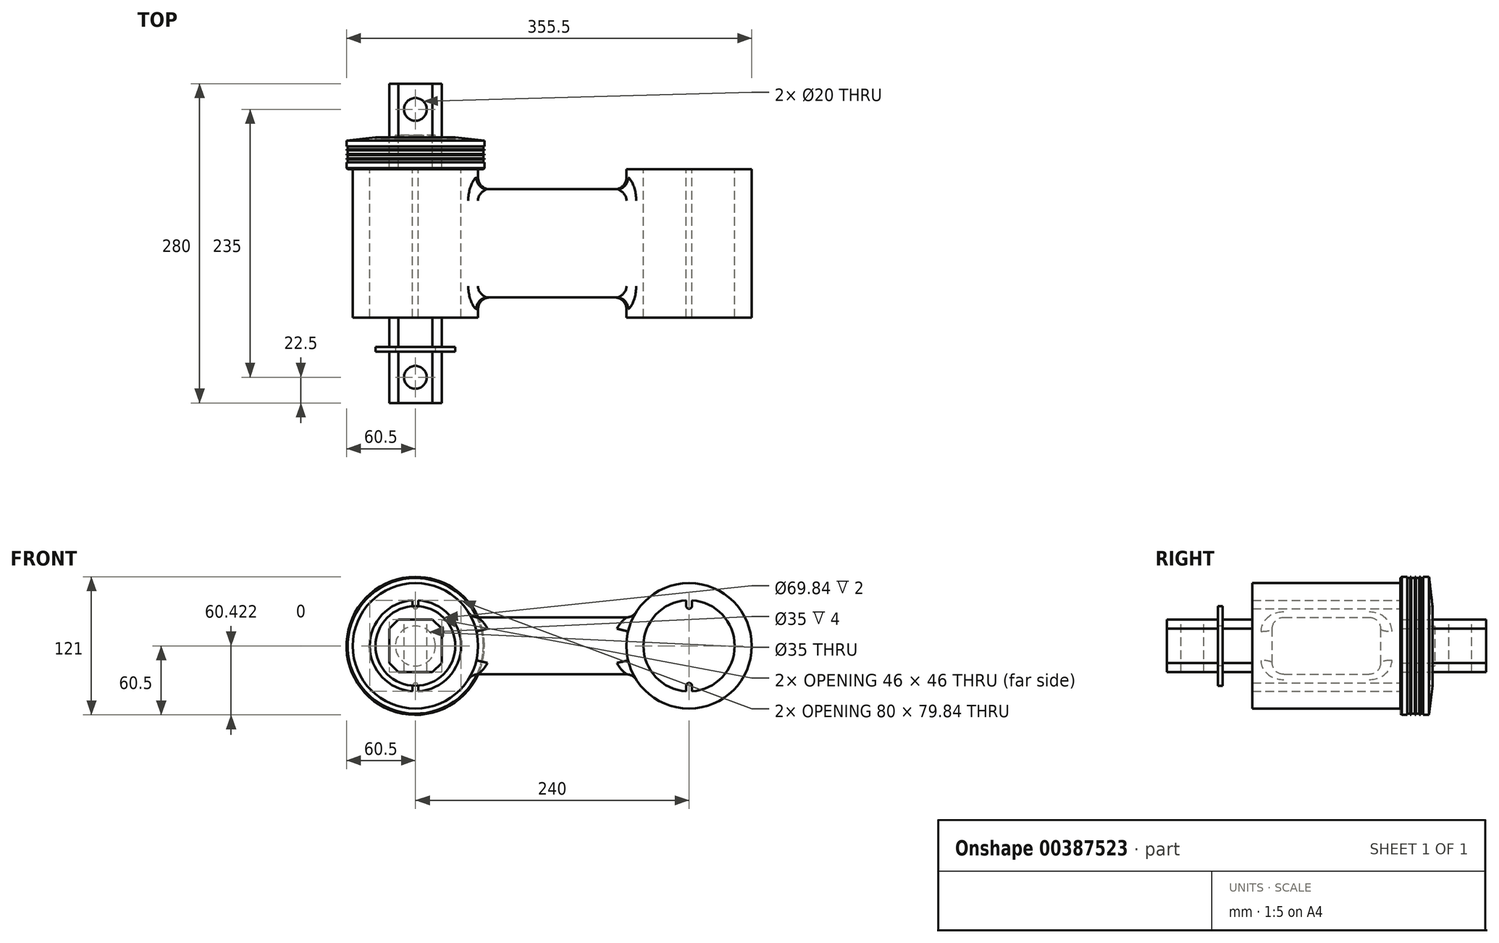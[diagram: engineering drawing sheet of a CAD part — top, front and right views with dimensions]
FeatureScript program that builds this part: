
annotation { "Feature Type Name" : "Feature", "Feature Type Description" : "" }
export const myFeature = defineFeature(function(context is Context, id is Id, definition is map)
    precondition{}
    {
        {
            var Q0;
            Q0=qCreatedBy(makeId("Front.planeOp"),FACE);
            var sketch = newSketch(context, id + "F0", { "sketchPlane" : qUnion([Q0])});
            skLineSegment(sketch, "E0", {"start": v(0, -75.22) * mm, "end": v(0, 75.8) * mm, "construction": true});
            skLineSegment(sketch, "E1.0", {"start": v(120, -75.22) * mm, "end": v(120, 75.8) * mm, "construction": true});
            skLineSegment(sketch, "E2.0", {"start": v(-120, -75.22) * mm, "end": v(-120, 75.8) * mm, "construction": true});
            skLineSegment(sketch, "E3", {"start": v(138.7, 0) * mm, "end": v(-135.83, 0) * mm, "construction": true});
            skLineSegment(sketch, "E4", {"start": v(-65.23, 25) * mm, "end": v(65.23, 25) * mm});
            skLineSegment(sketch, "E5.0", {"start": v(-65.23, -25) * mm, "end": v(65.23, -25) * mm});
            skPoint(sketch, "E6.visualSharp", {"position": v(-71.01, 25) * mm});
            skArc(sketch, "E6.filletArc", {"start": v(-73.65, 29.62) * mm, "mid": v(-70.03, 26.23) * mm, "end": v(-65.23, 25) * mm});
            skPoint(sketch, "E7.visualSharp", {"position": v(-71.01, -25) * mm});
            skArc(sketch, "E7.filletArc", {"start": v(-65.23, -25) * mm, "mid": v(-70.03, -26.23) * mm, "end": v(-73.65, -29.62) * mm});
            skPoint(sketch, "E8.visualSharp", {"position": v(71.01, 25) * mm});
            skArc(sketch, "E8.filletArc", {"start": v(65.23, 25) * mm, "mid": v(70.03, 26.23) * mm, "end": v(73.65, 29.62) * mm});
            skPoint(sketch, "E9.visualSharp", {"position": v(71.01, -25) * mm});
            skArc(sketch, "E9.filletArc", {"start": v(73.65, -29.62) * mm, "mid": v(70.03, -26.23) * mm, "end": v(65.23, -25) * mm});
            skCircle(sketch, "E10.converted", {"center": v(-120, 0) * mm, "radius": 55 * mm});
            skCircle(sketch, "E11.converted", {"center": v(120, 0) * mm, "radius": 55 * mm});
            skArc(sketch, "E12", {"start": v(-117.5, -39.92) * mm, "mid": v(-80, 0) * mm, "end": v(-117.5, 39.92) * mm});
            skArc(sketch, "E13", {"start": v(117.5, 39.92) * mm, "mid": v(80, 0) * mm, "end": v(117.5, -39.92) * mm});
            skArc(sketch, "E14", {"start": v(117.5, 35) * mm, "mid": v(120, 32.5) * mm, "end": v(122.5, 35) * mm});
            skLineSegment(sketch, "E15", {"start": v(122.5, 35) * mm, "end": v(122.5, 39.92) * mm});
            skLineSegment(sketch, "E16", {"start": v(117.5, 35) * mm, "end": v(117.5, 39.92) * mm});
            skArc(sketch, "E17.MirrorCS", {"start": v(117.5, -35) * mm, "mid": v(120, -32.5) * mm, "end": v(122.5, -35) * mm});
            skLineSegment(sketch, "E18.MirrorCS", {"start": v(122.5, -35) * mm, "end": v(122.5, -39.92) * mm});
            skLineSegment(sketch, "E19.MirrorCS", {"start": v(117.5, -35) * mm, "end": v(117.5, -39.92) * mm});
            skLineSegment(sketch, "E20.MirrorCS", {"start": v(-122.5, 35) * mm, "end": v(-122.5, 39.92) * mm});
            skLineSegment(sketch, "E21.MirrorCS", {"start": v(-117.5, 35) * mm, "end": v(-117.5, 39.92) * mm});
            skArc(sketch, "E22.MirrorCS", {"start": v(-117.5, 35) * mm, "mid": v(-120, 32.5) * mm, "end": v(-122.5, 35) * mm});
            skLineSegment(sketch, "E23.MirrorCS", {"start": v(-117.5, -35) * mm, "end": v(-117.5, -39.92) * mm});
            skArc(sketch, "E24.MirrorCS", {"start": v(-117.5, -35) * mm, "mid": v(-120, -32.5) * mm, "end": v(-122.5, -35) * mm});
            skLineSegment(sketch, "E25.MirrorCS", {"start": v(-122.5, -35) * mm, "end": v(-122.5, -39.92) * mm});
            skArc(sketch, "E26.trimOffspring", {"start": v(122.5, -39.92) * mm, "mid": v(160, 0) * mm, "end": v(122.5, 39.92) * mm});
            skArc(sketch, "E27.trimOffspring", {"start": v(-122.5, 39.92) * mm, "mid": v(-160, 0) * mm, "end": v(-122.5, -39.92) * mm});
            skSolve(sketch);
        }
        {
            var Q0;
            Q0=makeQuery(id+"F0.imprint","IMPRINT",FACE,{"disambiguationData":[TD([[makeQuery(id+"F0.imprint","IMPRINT",EDGE,{"derivedFrom":sQuery(id+"F0.wireOp",EDGE,"E12")}),-1.0]])]});
            var Q1;
            Q1=makeQuery(id+"F0.imprint","IMPRINT",FACE,{"disambiguationData":[TD([[makeQuery(id+"F0.imprint","IMPRINT",EDGE,{"derivedFrom":sQuery(id+"F0.wireOp",EDGE,"E13")}),-1.0]])]});
            extrude(context, id + "F1", {"entities" : qUnion([Q0, Q1]), "endBound" : BoundingType.SYMMETRIC, "depth" : 130 * mm});
        }
        {
            var Q0;
            Q0=makeQuery(id+"F0.imprint","IMPRINT",FACE,{"disambiguationData":[TD([[makeQuery(id+"F0.imprint","IMPRINT",EDGE,{"derivedFrom":sQuery(id+"F0.wireOp",EDGE,"E4")}),-1.0]])]});
            extrude(context, id + "F2", {"entities" : qUnion([Q0]), "operationType" : NewBodyOperationType.ADD, "endBound" : BoundingType.SYMMETRIC, "depth" : 95 * mm});
        }
        {
            var Q0;
            Q0=makeQuery(id+"F2.opExtrude","CAP_FACE",FACE,{"disambiguationData":[OSD([sQuery(id+"F0.wireOp",EDGE,"E4"),sQuery(id+"F0.wireOp",EDGE,"E5.0"),sQuery(id+"F0.wireOp",EDGE,"E6.filletArc"),sQuery(id+"F0.wireOp",EDGE,"E7.filletArc"),sQuery(id+"F0.wireOp",EDGE,"E8.filletArc"),sQuery(id+"F0.wireOp",EDGE,"E9.filletArc"),sQuery(id+"F0.wireOp",EDGE,"E10.converted"),sQuery(id+"F0.wireOp",EDGE,"E11.converted")])],"isStart":false});
            var Q1;
            Q1=makeQuery(id+"F2.opExtrude","CAP_FACE",FACE,{"disambiguationData":[OSD([sQuery(id+"F0.wireOp",EDGE,"E4"),sQuery(id+"F0.wireOp",EDGE,"E5.0"),sQuery(id+"F0.wireOp",EDGE,"E6.filletArc"),sQuery(id+"F0.wireOp",EDGE,"E7.filletArc"),sQuery(id+"F0.wireOp",EDGE,"E8.filletArc"),sQuery(id+"F0.wireOp",EDGE,"E9.filletArc"),sQuery(id+"F0.wireOp",EDGE,"E10.converted"),sQuery(id+"F0.wireOp",EDGE,"E11.converted")])],"isStart":true});
            fillet(context, id + "F3", {"entities" : qUnion([Q0, Q1]), "radius" : 10 * mm, "tangentPropagation" : true, "allowEdgeOverflow" : false});
        }
        {
            var Q0;
            Q0=qCreatedBy(makeId("Front.planeOp"),FACE);
            var sketch = newSketch(context, id + "F4", { "sketchPlane" : qUnion([Q0])});
            skArc(sketch, "E28.0", {"start": v(-117.5, -39.92) * mm, "mid": v(-80, 0) * mm, "end": v(-117.5, 39.92) * mm});
            skArc(sketch, "E28.1", {"start": v(117.5, 39.92) * mm, "mid": v(80, 0) * mm, "end": v(117.5, -39.92) * mm});
            skLineSegment(sketch, "E29.1", {"start": v(-117.5, 35) * mm, "end": v(-117.5, 39.92) * mm});
            skArc(sketch, "E29.2", {"start": v(-117.5, 35) * mm, "mid": v(-120, 32.5) * mm, "end": v(-122.5, 35) * mm});
            skLineSegment(sketch, "E29.3", {"start": v(-122.5, 35) * mm, "end": v(-122.5, 39.92) * mm});
            skArc(sketch, "E29.4", {"start": v(-122.5, 39.92) * mm, "mid": v(-160, 0) * mm, "end": v(-122.5, -39.92) * mm});
            skLineSegment(sketch, "E29.5", {"start": v(-122.5, -35) * mm, "end": v(-122.5, -39.92) * mm});
            skArc(sketch, "E29.6", {"start": v(-117.5, -35) * mm, "mid": v(-120, -32.5) * mm, "end": v(-122.5, -35) * mm});
            skLineSegment(sketch, "E29.7", {"start": v(-117.5, -35) * mm, "end": v(-117.5, -39.92) * mm});
            skLineSegment(sketch, "E30.1", {"start": v(117.5, 35) * mm, "end": v(117.5, 39.92) * mm});
            skLineSegment(sketch, "E30.2", {"start": v(122.5, 35) * mm, "end": v(122.5, 39.92) * mm});
            skArc(sketch, "E30.3", {"start": v(117.5, 35) * mm, "mid": v(120, 32.5) * mm, "end": v(122.5, 35) * mm});
            skArc(sketch, "E30.4", {"start": v(122.5, -39.92) * mm, "mid": v(160, 0) * mm, "end": v(122.5, 39.92) * mm});
            skLineSegment(sketch, "E30.5", {"start": v(122.5, -35) * mm, "end": v(122.5, -39.92) * mm});
            skArc(sketch, "E30.6", {"start": v(117.5, -35) * mm, "mid": v(120, -32.5) * mm, "end": v(122.5, -35) * mm});
            skLineSegment(sketch, "E30.7", {"start": v(117.5, -35) * mm, "end": v(117.5, -39.92) * mm});
            skSolve(sketch);
        }
        {
            var Q0;
            Q0=makeQuery(id+"F4.imprint","IMPRINT",FACE,{"disambiguationData":[TD([[makeQuery(id+"F4.imprint","IMPRINT",EDGE,{"derivedFrom":sQuery(id+"F4.wireOp",EDGE,"E28.1")}),1.0]])]});
            var Q1;
            Q1=makeQuery(id+"F4.imprint","IMPRINT",FACE,{"disambiguationData":[TD([[makeQuery(id+"F4.imprint","IMPRINT",EDGE,{"derivedFrom":sQuery(id+"F4.wireOp",EDGE,"E28.0")}),1.0]])]});
            extrude(context, id + "F5", {"entities" : qUnion([Q0, Q1]), "endBound" : BoundingType.SYMMETRIC, "depth" : 130 * mm});
        }
        {
            var Q0;
            Q0=qCreatedBy(makeId("Front.planeOp"),FACE);
            var sketch = newSketch(context, id + "F6", { "sketchPlane" : qUnion([Q0])});
            skCircle(sketch, "E31.0", {"center": v(-120, 0) * mm, "radius": 55 * mm, "construction": true});
            skCircle(sketch, "E32.0", {"center": v(120, 0) * mm, "radius": 55 * mm, "construction": true});
            skLineSegment(sketch, "E33.bottom", {"start": v(-105, -23) * mm, "end": v(-135, -23) * mm});
            skLineSegment(sketch, "E33.top", {"start": v(-105, 23) * mm, "end": v(-135, 23) * mm});
            skLineSegment(sketch, "E33.left", {"start": v(-97, -15) * mm, "end": v(-97, 15) * mm});
            skLineSegment(sketch, "E33.right", {"start": v(-143, -15) * mm, "end": v(-143, 15) * mm});
            skLineSegment(sketch, "E34", {"start": v(-120, 29.37) * mm, "end": v(-120, -29.52) * mm, "construction": true});
            skPoint(sketch, "E34.endSnap0", {"position": v(-120, 23) * mm});
            skLineSegment(sketch, "E35.0", {"start": v(-135, 29.37) * mm, "end": v(-135, -29.52) * mm, "construction": true});
            skLineSegment(sketch, "E36.0", {"start": v(-105, 29.37) * mm, "end": v(-105, -29.52) * mm, "construction": true});
            skLineSegment(sketch, "E37", {"start": v(0, 0) * mm, "end": v(0, -57.4) * mm, "construction": true});
            skLineSegment(sketch, "E38", {"start": v(-146.66, 0) * mm, "end": v(-89.7, 0) * mm, "construction": true});
            skLineSegment(sketch, "E39.0", {"start": v(-146.66, 15) * mm, "end": v(-89.7, 15) * mm, "construction": true});
            skLineSegment(sketch, "E40.0", {"start": v(-146.66, -15) * mm, "end": v(-89.7, -15) * mm, "construction": true});
            skArc(sketch, "E41.0", {"start": v(-127.46, -34.2) * mm, "mid": v(-120, -27.5) * mm, "end": v(-112.54, -34.2) * mm});
            skArc(sketch, "E41.1", {"start": v(-127.46, 34.2) * mm, "mid": v(-155, 0) * mm, "end": v(-127.46, -34.2) * mm});
            skArc(sketch, "E41.2", {"start": v(-112.54, 34.2) * mm, "mid": v(-120, 27.5) * mm, "end": v(-127.46, 34.2) * mm});
            skArc(sketch, "E41.3", {"start": v(-112.54, -34.2) * mm, "mid": v(-85, 0) * mm, "end": v(-112.54, 34.2) * mm});
            skLineSegment(sketch, "E42", {"start": v(-143, 15) * mm, "end": v(-135, 23) * mm});
            skLineSegment(sketch, "E43", {"start": v(-105, 23) * mm, "end": v(-97, 15) * mm});
            skLineSegment(sketch, "E44", {"start": v(-143, -15) * mm, "end": v(-135, -23) * mm});
            skLineSegment(sketch, "E45", {"start": v(-105, -23) * mm, "end": v(-97, -15) * mm});
            skPoint(sketch, "E46.orphan", {"position": v(-97, -23) * mm});
            skPoint(sketch, "E47.orphan", {"position": v(-97, 23) * mm});
            skPoint(sketch, "E48.orphan", {"position": v(-143, 23) * mm});
            skPoint(sketch, "E49.orphan", {"position": v(-143, -23) * mm});
            skLineSegment(sketch, "E50.MirrorCS", {"start": v(105, 23) * mm, "end": v(97, 15) * mm});
            skLineSegment(sketch, "E51.MirrorCS", {"start": v(105, -23) * mm, "end": v(97, -15) * mm});
            skLineSegment(sketch, "E52.MirrorCS", {"start": v(143, -15) * mm, "end": v(143, 15) * mm});
            skLineSegment(sketch, "E53.MirrorCS", {"start": v(105, 23) * mm, "end": v(135, 23) * mm});
            skLineSegment(sketch, "E54.MirrorCS", {"start": v(105, -23) * mm, "end": v(135, -23) * mm});
            skPoint(sketch, "E55.MirrorP", {"position": v(97, 23) * mm});
            skPoint(sketch, "E56.MirrorP", {"position": v(120, 23) * mm});
            skPoint(sketch, "E57.MirrorP", {"position": v(97, -23) * mm});
            skLineSegment(sketch, "E58.MirrorCS", {"start": v(97, -15) * mm, "end": v(97, 15) * mm});
            skLineSegment(sketch, "E59.MirrorCS", {"start": v(143, -15) * mm, "end": v(135, -23) * mm});
            skLineSegment(sketch, "E60.MirrorCS", {"start": v(143, 15) * mm, "end": v(135, 23) * mm});
            skSolve(sketch);
        }
        {
            var Q0;
            Q0=makeQuery(id+"F6.imprint","IMPRINT",FACE,{"disambiguationData":[TD([[makeQuery(id+"F6.imprint","IMPRINT",EDGE,{"derivedFrom":sQuery(id+"F6.wireOp",EDGE,"E33.bottom")}),-1.0]])]});
            extrude(context, id + "F7", {"entities" : qUnion([Q0]), "operationType" : NewBodyOperationType.ADD, "endBound" : BoundingType.SYMMETRIC, "depth" : 280 * mm});
        }
        {
            var Q0;
            Q0=makeQuery(id+"F6.imprint","IMPRINT",FACE,{"disambiguationData":[TD([[makeQuery(id+"F6.imprint","IMPRINT",EDGE,{"derivedFrom":sQuery(id+"F6.wireOp",EDGE,"E50.MirrorCS")}),1.0]])]});
            extrude(context, id + "F8", {"entities" : qUnion([Q0]), "operationType" : NewBodyOperationType.ADD, "endBound" : BoundingType.SYMMETRIC, "depth" : 280 * mm});
        }
        {
            var Q0;
            Q0=makeQuery(id+"F7.opExtrude","CAP_FACE",FACE,{"disambiguationData":[OSD([sQuery(id+"F6.wireOp",EDGE,"E33.bottom"),sQuery(id+"F6.wireOp",EDGE,"E33.top"),sQuery(id+"F6.wireOp",EDGE,"E33.left"),sQuery(id+"F6.wireOp",EDGE,"E33.right"),sQuery(id+"F6.wireOp",EDGE,"E42"),sQuery(id+"F6.wireOp",EDGE,"E43"),sQuery(id+"F6.wireOp",EDGE,"E44"),sQuery(id+"F6.wireOp",EDGE,"E45")])],"isStart":false});
            cPlane(context, id + "F9", {"entities" : qUnion([Q0]), "cplaneType" : CPlaneType.OFFSET, "offset" : 45 * mm, "oppositeDirection" : true, "width" : 150 * mm, "height" : 150 * mm});
        }
        {
            var Q0;
            Q0=qCreatedBy(id+"F9.planeOp",FACE);
            var sketch = newSketch(context, id + "F10", { "sketchPlane" : qUnion([Q0])});
            skPoint(sketch, "E61.0", {"position": v(-120, -0.08) * mm});
            skCircle(sketch, "E62", {"center": v(-120, -0.08) * mm, "radius": 35 * mm});
            skCircle(sketch, "E63", {"center": v(-120, -0.08) * mm, "radius": 17.5 * mm});
            skCircle(sketch, "E64.MirrorC", {"center": v(120, -0.08) * mm, "radius": 17.5 * mm});
            skCircle(sketch, "E65.MirrorC", {"center": v(120, -0.08) * mm, "radius": 35 * mm});
            skSolve(sketch);
        }
        {
            var Q0;
            Q0=makeQuery(id+"F10.imprint","IMPRINT",FACE,{"disambiguationData":[TD([[makeQuery(id+"F10.imprint","IMPRINT",EDGE,{"derivedFrom":sQuery(id+"F10.wireOp",EDGE,"E62")}),1.0]])]});
            extrude(context, id + "F11", {"entities" : qUnion([Q0]), "oppositeDirection" : true, "depth" : 4 * mm});
        }
        {
            var Q0;
            Q0=makeQuery(id+"F10.imprint","IMPRINT",FACE,{"disambiguationData":[TD([[makeQuery(id+"F10.imprint","IMPRINT",EDGE,{"derivedFrom":sQuery(id+"F10.wireOp",EDGE,"E64.MirrorC")}),1.0]])]});
            extrude(context, id + "F12", {"entities" : qUnion([Q0]), "oppositeDirection" : true, "depth" : 4 * mm});
        }
        {
            var Q0;
            Q0=makeQuery(id+"F8.opExtrude","CAP_FACE",FACE,{"disambiguationData":[OSD([sQuery(id+"F6.wireOp",EDGE,"E50.MirrorCS"),sQuery(id+"F6.wireOp",EDGE,"E51.MirrorCS"),sQuery(id+"F6.wireOp",EDGE,"E52.MirrorCS"),sQuery(id+"F6.wireOp",EDGE,"E53.MirrorCS"),sQuery(id+"F6.wireOp",EDGE,"E54.MirrorCS"),sQuery(id+"F6.wireOp",EDGE,"E58.MirrorCS"),sQuery(id+"F6.wireOp",EDGE,"E59.MirrorCS"),sQuery(id+"F6.wireOp",EDGE,"E60.MirrorCS")])],"isStart":true});
            cPlane(context, id + "F13", {"entities" : qUnion([Q0]), "cplaneType" : CPlaneType.OFFSET, "offset" : 45 * mm, "oppositeDirection" : true, "width" : 150 * mm, "height" : 150 * mm});
        }
        {
            var Q0;
            Q0=qCreatedBy(id+"F13.planeOp",FACE);
            var sketch = newSketch(context, id + "F14", { "sketchPlane" : qUnion([Q0])});
            skCircle(sketch, "E66.0", {"center": v(-120, -0.08) * mm, "radius": 17.5 * mm});
            skCircle(sketch, "E67.0", {"center": v(-120, -0.08) * mm, "radius": 35 * mm});
            skCircle(sketch, "E68.0", {"center": v(120, -0.08) * mm, "radius": 17.5 * mm});
            skCircle(sketch, "E69.0", {"center": v(120, -0.08) * mm, "radius": 35 * mm});
            skSolve(sketch);
        }
        {
            var Q0;
            Q0=makeQuery(id+"F14.imprint","IMPRINT",FACE,{"disambiguationData":[TD([[makeQuery(id+"F14.imprint","IMPRINT",EDGE,{"derivedFrom":sQuery(id+"F14.wireOp",EDGE,"E66.0")}),-1.0]])]});
            var Q1;
            Q1=makeQuery(id+"F14.imprint","IMPRINT",FACE,{"disambiguationData":[TD([[makeQuery(id+"F14.imprint","IMPRINT",EDGE,{"derivedFrom":sQuery(id+"F14.wireOp",EDGE,"E68.0")}),1.0]])]});
            extrude(context, id + "F15", {"entities" : qUnion([Q0, Q1]), "oppositeDirection" : true, "depth" : 4 * mm});
        }
        {
            var Q0;
            Q0=makeQuery(id+"F12.opExtrude","SWEPT_BODY",BODY,{"disambiguationData":[OSD([sQuery(id+"F10.wireOp",EDGE,"E64.MirrorC"),sQuery(id+"F10.wireOp",EDGE,"E65.MirrorC")])]});
            var Q1;
            Q1=makeQuery(id+"F15.opExtrude","SWEPT_BODY",BODY,{"disambiguationData":[OSD([sQuery(id+"F14.wireOp",EDGE,"E66.0"),sQuery(id+"F14.wireOp",EDGE,"E67.0")])]});
            var Q2;
            Q2=makeQuery(id+"F5.opExtrude","SWEPT_BODY",BODY,{"disambiguationData":[OSD([sQuery(id+"F4.wireOp",EDGE,"E28.1"),sQuery(id+"F4.wireOp",EDGE,"E30.1"),sQuery(id+"F4.wireOp",EDGE,"E30.2"),sQuery(id+"F4.wireOp",EDGE,"E30.3"),sQuery(id+"F4.wireOp",EDGE,"E30.4"),sQuery(id+"F4.wireOp",EDGE,"E30.5"),sQuery(id+"F4.wireOp",EDGE,"E30.6"),sQuery(id+"F4.wireOp",EDGE,"E30.7")])]});
            booleanBodies(context, id + "F16", {"operationType" : BooleanOperationType.SUBTRACTION, "tools" : qUnion([Q0, Q1]), "targets" : qUnion([Q2]), "keepTools" : true});
        }
        {
            var Q0;
            Q0=makeQuery(id+"F15.opExtrude","SWEPT_BODY",BODY,{"disambiguationData":[OSD([sQuery(id+"F14.wireOp",EDGE,"E68.0"),sQuery(id+"F14.wireOp",EDGE,"E69.0")])]});
            var Q1;
            Q1=makeQuery(id+"F11.opExtrude","SWEPT_BODY",BODY,{"disambiguationData":[OSD([sQuery(id+"F10.wireOp",EDGE,"E62"),sQuery(id+"F10.wireOp",EDGE,"E63")])]});
            var Q2;
            Q2=makeQuery(id+"F5.opExtrude","SWEPT_BODY",BODY,{"disambiguationData":[OSD([sQuery(id+"F4.wireOp",EDGE,"E28.0"),sQuery(id+"F4.wireOp",EDGE,"E29.1"),sQuery(id+"F4.wireOp",EDGE,"E29.2"),sQuery(id+"F4.wireOp",EDGE,"E29.3"),sQuery(id+"F4.wireOp",EDGE,"E29.4"),sQuery(id+"F4.wireOp",EDGE,"E29.5"),sQuery(id+"F4.wireOp",EDGE,"E29.6"),sQuery(id+"F4.wireOp",EDGE,"E29.7")])]});
            booleanBodies(context, id + "F17", {"operationType" : BooleanOperationType.SUBTRACTION, "tools" : qUnion([Q0, Q1]), "targets" : qUnion([Q2]), "keepTools" : true});
        }
        {
            var Q0;
            Q0=qCreatedBy(makeId("Top.planeOp"),FACE);
            var sketch = newSketch(context, id + "F18", { "sketchPlane" : qUnion([Q0])});
            skPoint(sketch, "E70.0", {"position": v(-120, -140) * mm});
            skPoint(sketch, "E71.0", {"position": v(-120, 140) * mm});
            skPoint(sketch, "E72.0", {"position": v(120, 140) * mm});
            skPoint(sketch, "E73.0", {"position": v(120, -140) * mm});
            skCircle(sketch, "E74", {"center": v(-120, 117.5) * mm, "radius": 10 * mm});
            skCircle(sketch, "E75.MirrorC", {"center": v(-120, -117.5) * mm, "radius": 10 * mm});
            skCircle(sketch, "E76.MirrorC", {"center": v(120, 117.5) * mm, "radius": 10 * mm});
            skCircle(sketch, "E77.MirrorC", {"center": v(120, -117.5) * mm, "radius": 10 * mm});
            skSolve(sketch);
        }
        {
            var Q0;
            Q0=qSketchRegion(id+"F18",true);
            var Q1;
            Q1=sQuery(id+"F18.wireOp",EDGE,"E74");
            var Q2;
            Q2=sQuery(id+"F18.wireOp",EDGE,"E76.MirrorC");
            var Q3;
            Q3=sQuery(id+"F18.wireOp",EDGE,"E77.MirrorC");
            var Q4;
            Q4=sQuery(id+"F18.wireOp",EDGE,"E75.MirrorC");
            extrude(context, id + "F19", {"entities" : qUnion([Q0]), "operationType" : NewBodyOperationType.REMOVE, "surfaceEntities" : qUnion([Q1, Q2, Q3, Q4]), "endBound" : BoundingType.SYMMETRIC, "oppositeDirection" : true, "depth" : 100 * mm});
        }
        {
            var Q0;
            {var subQ2=sQuery(id+"F6.wireOp",EDGE,"E33.right");Q0=makeQuery(id+"F17.opBoolean","SPLIT",FACE,{"disambiguationData":[TD([makeQuery(id+"F15.opExtrude","CAP_FACE",FACE,{"disambiguationData":[OSD([sQuery(id+"F14.wireOp",EDGE,"E68.0"),sQuery(id+"F14.wireOp",EDGE,"E69.0")])],"isStart":true})])],"derivedFrom":makeQuery(id+"F7.boolean.opBoolean","SPLIT",FACE,{"disambiguationData":[TD([makeQuery(id+"F5.opExtrude","CAP_FACE",FACE,{"disambiguationData":[OSD([sQuery(id+"F4.wireOp",EDGE,"E28.0"),sQuery(id+"F4.wireOp",EDGE,"E29.1"),sQuery(id+"F4.wireOp",EDGE,"E29.2"),sQuery(id+"F4.wireOp",EDGE,"E29.3"),sQuery(id+"F4.wireOp",EDGE,"E29.4"),sQuery(id+"F4.wireOp",EDGE,"E29.5"),sQuery(id+"F4.wireOp",EDGE,"E29.6"),sQuery(id+"F4.wireOp",EDGE,"E29.7")])],"isStart":true})])],"derivedFrom":makeQuery(id+"F7.opExtrude","SWEPT_FACE",FACE,{"disambiguationData":[OSD([subQ2])]})})});}
            var Q1;
            {var subQ2=sQuery(id+"F6.wireOp",EDGE,"E33.left");Q1=makeQuery(id+"F17.opBoolean","SPLIT",FACE,{"disambiguationData":[TD([makeQuery(id+"F11.opExtrude","CAP_FACE",FACE,{"disambiguationData":[OSD([sQuery(id+"F10.wireOp",EDGE,"E62"),sQuery(id+"F10.wireOp",EDGE,"E63")])],"isStart":true})])],"derivedFrom":makeQuery(id+"F7.boolean.opBoolean","SPLIT",FACE,{"disambiguationData":[TD([makeQuery(id+"F5.opExtrude","CAP_FACE",FACE,{"disambiguationData":[OSD([sQuery(id+"F4.wireOp",EDGE,"E28.0"),sQuery(id+"F4.wireOp",EDGE,"E29.1"),sQuery(id+"F4.wireOp",EDGE,"E29.2"),sQuery(id+"F4.wireOp",EDGE,"E29.3"),sQuery(id+"F4.wireOp",EDGE,"E29.4"),sQuery(id+"F4.wireOp",EDGE,"E29.5"),sQuery(id+"F4.wireOp",EDGE,"E29.6"),sQuery(id+"F4.wireOp",EDGE,"E29.7")])],"isStart":false})])],"derivedFrom":makeQuery(id+"F7.opExtrude","SWEPT_FACE",FACE,{"disambiguationData":[OSD([subQ2])]})})});}
            cPlane(context, id + "F20", {"entities" : qUnion([Q0, Q1]), "cplaneType" : CPlaneType.MID_PLANE, "offset" : 25 * mm, "width" : 150 * mm, "height" : 150 * mm});
        }
        {
            var Q0;
            Q0=qCreatedBy(id+"F20.planeOp",FACE);
            var sketch = newSketch(context, id + "F21", { "sketchPlane" : qUnion([Q0])});
            skPoint(sketch, "E78.0", {"position": v(-140, 0) * mm});
            skPoint(sketch, "E79.0", {"position": v(140, 0) * mm});
            skLineSegment(sketch, "E80", {"start": v(-140, 0) * mm, "end": v(140, 0) * mm, "construction": true});
            skLineSegment(sketch, "E81.0", {"start": v(-91, 60.5) * mm, "end": v(-91, -35.08) * mm, "construction": true});
            skPoint(sketch, "E82.orphan", {"position": v(-91, 34.92) * mm});
            skPoint(sketch, "E83.orphan", {"position": v(91, 34.92) * mm});
            skLineSegment(sketch, "E84.0", {"start": v(-65, 60.5) * mm, "end": v(-65, -55) * mm, "construction": true});
            skPoint(sketch, "E85.orphan", {"position": v(-65, 55) * mm});
            skPoint(sketch, "E86.orphan", {"position": v(65, 55) * mm});
            skLineSegment(sketch, "E87.0", {"start": v(-93, 60.5) * mm, "end": v(-93, -35.08) * mm, "construction": true});
            skLineSegment(sketch, "E88.0", {"start": v(-90, 60.5) * mm, "end": v(-90, -35.08) * mm, "construction": true});
            skLineSegment(sketch, "E89.0", {"start": v(-85, 60.5) * mm, "end": v(-85, -35.08) * mm, "construction": true});
            skLineSegment(sketch, "E90.0", {"start": v(-66, 60.5) * mm, "end": v(-66, -55) * mm, "construction": true});
            skLineSegment(sketch, "E91.0", {"start": v(-71, 60.5) * mm, "end": v(-71, -55) * mm, "construction": true});
            skLineSegment(sketch, "E92.0", {"start": v(-82.5, 60.5) * mm, "end": v(-82.5, -35.08) * mm, "construction": true});
            skLineSegment(sketch, "E93.0", {"start": v(-81.5, 60.5) * mm, "end": v(-81.5, -35.08) * mm, "construction": true});
            skLineSegment(sketch, "E94.0", {"start": v(-78.5, 60.5) * mm, "end": v(-78.5, -35.08) * mm, "construction": true});
            skLineSegment(sketch, "E95.0", {"start": v(-77.5, 60.5) * mm, "end": v(-77.5, -35.08) * mm, "construction": true});
            skLineSegment(sketch, "E96.0", {"start": v(-74.5, 60.5) * mm, "end": v(-74.5, -35.08) * mm, "construction": true});
            skLineSegment(sketch, "E97.0", {"start": v(-73.5, 60.5) * mm, "end": v(-73.5, -35.08) * mm, "construction": true});
            skLineSegment(sketch, "E98.0", {"start": v(-140, 39.5) * mm, "end": v(140, 39.5) * mm, "construction": true});
            skLineSegment(sketch, "E99", {"start": v(-90, 60.5) * mm, "end": v(-85, 60.5) * mm});
            skLineSegment(sketch, "E100", {"start": v(-85, 59.5) * mm, "end": v(-82.5, 59.5) * mm});
            skLineSegment(sketch, "E101", {"start": v(-82.5, 59.5) * mm, "end": v(-82.5, 60.5) * mm});
            skLineSegment(sketch, "E102", {"start": v(-81.5, 60.5) * mm, "end": v(-81.5, 59.5) * mm});
            skLineSegment(sketch, "E103", {"start": v(-81.5, 59.5) * mm, "end": v(-78.5, 59.5) * mm});
            skLineSegment(sketch, "E104", {"start": v(-78.5, 59.5) * mm, "end": v(-78.5, 60.5) * mm});
            skLineSegment(sketch, "E105", {"start": v(-77.5, 60.5) * mm, "end": v(-77.5, 59.5) * mm});
            skLineSegment(sketch, "E106", {"start": v(-77.5, 59.5) * mm, "end": v(-74.5, 59.5) * mm});
            skLineSegment(sketch, "E107", {"start": v(-74.5, 59.5) * mm, "end": v(-74.5, 60.5) * mm});
            skLineSegment(sketch, "E108", {"start": v(-73.5, 60.5) * mm, "end": v(-73.5, 59.5) * mm});
            skLineSegment(sketch, "E109", {"start": v(-73.5, 59.5) * mm, "end": v(-71, 59.5) * mm});
            skLineSegment(sketch, "E110", {"start": v(-71, 59.5) * mm, "end": v(-71, 60.5) * mm});
            skLineSegment(sketch, "E111", {"start": v(-66, 60.5) * mm, "end": v(-65, 59.5) * mm});
            skLineSegment(sketch, "E112", {"start": v(-65, 59.5) * mm, "end": v(-65, 0) * mm});
            skLineSegment(sketch, "E113", {"start": v(-65, 0) * mm, "end": v(-91, 0) * mm});
            skLineSegment(sketch, "E114", {"start": v(-91, 0) * mm, "end": v(-91, 34.92) * mm});
            skLineSegment(sketch, "E115", {"start": v(-85, 60.5) * mm, "end": v(-85, 59.5) * mm});
            skLineSegment(sketch, "E116", {"start": v(-82.5, 60.5) * mm, "end": v(-81.5, 60.5) * mm});
            skLineSegment(sketch, "E117", {"start": v(-78.5, 60.5) * mm, "end": v(-77.5, 60.5) * mm});
            skLineSegment(sketch, "E118", {"start": v(-74.5, 60.5) * mm, "end": v(-73.5, 60.5) * mm});
            skLineSegment(sketch, "E119", {"start": v(-71, 60.5) * mm, "end": v(-66, 60.5) * mm});
            skLineSegment(sketch, "E120", {"start": v(-95, 34.92) * mm, "end": v(-91, 34.92) * mm, "construction": true});
            skLineSegment(sketch, "E121", {"start": v(-91, 34.92) * mm, "end": v(-93, 34.92) * mm});
            skLineSegment(sketch, "E122", {"start": v(-93, 34.92) * mm, "end": v(-90, 60.5) * mm});
            skLineSegment(sketch, "E123.MirrorCS", {"start": v(74.5, 59.5) * mm, "end": v(74.5, 60.5) * mm});
            skLineSegment(sketch, "E124.MirrorCS", {"start": v(73.5, 60.5) * mm, "end": v(73.5, 59.5) * mm});
            skLineSegment(sketch, "E125.MirrorCS", {"start": v(74.5, 60.5) * mm, "end": v(73.5, 60.5) * mm});
            skLineSegment(sketch, "E126.MirrorCS", {"start": v(78.5, 59.5) * mm, "end": v(78.5, 60.5) * mm});
            skLineSegment(sketch, "E127.MirrorCS", {"start": v(81.5, 59.5) * mm, "end": v(78.5, 59.5) * mm});
            skLineSegment(sketch, "E128.MirrorCS", {"start": v(77.5, 60.5) * mm, "end": v(77.5, 59.5) * mm});
            skLineSegment(sketch, "E129.MirrorCS", {"start": v(82.5, 59.5) * mm, "end": v(82.5, 60.5) * mm});
            skLineSegment(sketch, "E130.MirrorCS", {"start": v(78.5, 60.5) * mm, "end": v(77.5, 60.5) * mm});
            skLineSegment(sketch, "E131.MirrorCS", {"start": v(81.5, 60.5) * mm, "end": v(81.5, 59.5) * mm});
            skLineSegment(sketch, "E132.MirrorCS", {"start": v(82.5, 60.5) * mm, "end": v(81.5, 60.5) * mm});
            skLineSegment(sketch, "E133.MirrorCS", {"start": v(77.5, 59.5) * mm, "end": v(74.5, 59.5) * mm});
            skLineSegment(sketch, "E134.MirrorCS", {"start": v(85, 60.5) * mm, "end": v(85, 59.5) * mm});
            skLineSegment(sketch, "E135.MirrorCS", {"start": v(71, 59.5) * mm, "end": v(71, 60.5) * mm});
            skLineSegment(sketch, "E136.MirrorCS", {"start": v(73.5, 59.5) * mm, "end": v(71, 59.5) * mm});
            skLineSegment(sketch, "E137.MirrorCS", {"start": v(85, 59.5) * mm, "end": v(82.5, 59.5) * mm});
            skLineSegment(sketch, "E138.MirrorCS", {"start": v(66, 60.5) * mm, "end": v(65, 59.5) * mm});
            skLineSegment(sketch, "E139.MirrorCS", {"start": v(91, 34.92) * mm, "end": v(93, 34.92) * mm});
            skLineSegment(sketch, "E140.MirrorCS", {"start": v(95, 34.92) * mm, "end": v(91, 34.92) * mm, "construction": true});
            skLineSegment(sketch, "E141.MirrorCS", {"start": v(91, 0) * mm, "end": v(91, 34.92) * mm});
            skLineSegment(sketch, "E142.MirrorCS", {"start": v(71, 60.5) * mm, "end": v(66, 60.5) * mm});
            skLineSegment(sketch, "E143.MirrorCS", {"start": v(90, 60.5) * mm, "end": v(85, 60.5) * mm});
            skLineSegment(sketch, "E144.MirrorCS", {"start": v(65, 0) * mm, "end": v(91, 0) * mm});
            skLineSegment(sketch, "E145.MirrorCS", {"start": v(65, 59.5) * mm, "end": v(65, 0) * mm});
            skLineSegment(sketch, "E146.MirrorCS", {"start": v(93, 34.92) * mm, "end": v(90, 60.5) * mm});
            skSolve(sketch);
        }
        {
            var Q0;
            Q0=qSketchRegion(id+"F21",true);
            var Q1;
            Q1=sQuery(id+"F21.wireOp",EDGE,"E80");
            revolve(context, id + "F22", {"entities" : qUnion([Q0]), "axis" : qUnion([Q1]), "revolveType" : RevolveType.FULL});
        }
        {
            var Q0;
            Q0=makeQuery(id+"F5.opExtrude","SWEPT_BODY",BODY,{"disambiguationData":[OSD([sQuery(id+"F4.wireOp",EDGE,"E28.0"),sQuery(id+"F4.wireOp",EDGE,"E29.1"),sQuery(id+"F4.wireOp",EDGE,"E29.2"),sQuery(id+"F4.wireOp",EDGE,"E29.3"),sQuery(id+"F4.wireOp",EDGE,"E29.4"),sQuery(id+"F4.wireOp",EDGE,"E29.5"),sQuery(id+"F4.wireOp",EDGE,"E29.6"),sQuery(id+"F4.wireOp",EDGE,"E29.7")])]});
            var Q1;
            Q1=makeQuery(id+"F22.opRevolve","SWEPT_BODY",BODY,{"disambiguationData":[OSD([sQuery(id+"F21.wireOp",EDGE,"E99"),sQuery(id+"F21.wireOp",EDGE,"E100"),sQuery(id+"F21.wireOp",EDGE,"E101"),sQuery(id+"F21.wireOp",EDGE,"E102"),sQuery(id+"F21.wireOp",EDGE,"E103"),sQuery(id+"F21.wireOp",EDGE,"E104"),sQuery(id+"F21.wireOp",EDGE,"E105"),sQuery(id+"F21.wireOp",EDGE,"E106"),sQuery(id+"F21.wireOp",EDGE,"E107"),sQuery(id+"F21.wireOp",EDGE,"E108"),sQuery(id+"F21.wireOp",EDGE,"E109"),sQuery(id+"F21.wireOp",EDGE,"E110"),sQuery(id+"F21.wireOp",EDGE,"E111"),sQuery(id+"F21.wireOp",EDGE,"E112"),sQuery(id+"F21.wireOp",EDGE,"E113"),sQuery(id+"F21.wireOp",EDGE,"E114"),sQuery(id+"F21.wireOp",EDGE,"E115"),sQuery(id+"F21.wireOp",EDGE,"E116"),sQuery(id+"F21.wireOp",EDGE,"E117"),sQuery(id+"F21.wireOp",EDGE,"E118"),sQuery(id+"F21.wireOp",EDGE,"E119"),sQuery(id+"F21.wireOp",EDGE,"E121"),sQuery(id+"F21.wireOp",EDGE,"E122")])]});
            var Q2;
            Q2=makeQuery(id+"F22.opRevolve","SWEPT_BODY",BODY,{"disambiguationData":[OSD([sQuery(id+"F21.wireOp",EDGE,"E123.MirrorCS"),sQuery(id+"F21.wireOp",EDGE,"E124.MirrorCS"),sQuery(id+"F21.wireOp",EDGE,"E125.MirrorCS"),sQuery(id+"F21.wireOp",EDGE,"E126.MirrorCS"),sQuery(id+"F21.wireOp",EDGE,"E127.MirrorCS"),sQuery(id+"F21.wireOp",EDGE,"E128.MirrorCS"),sQuery(id+"F21.wireOp",EDGE,"E129.MirrorCS"),sQuery(id+"F21.wireOp",EDGE,"E130.MirrorCS"),sQuery(id+"F21.wireOp",EDGE,"E131.MirrorCS"),sQuery(id+"F21.wireOp",EDGE,"E132.MirrorCS"),sQuery(id+"F21.wireOp",EDGE,"E133.MirrorCS"),sQuery(id+"F21.wireOp",EDGE,"E134.MirrorCS"),sQuery(id+"F21.wireOp",EDGE,"E135.MirrorCS"),sQuery(id+"F21.wireOp",EDGE,"E136.MirrorCS"),sQuery(id+"F21.wireOp",EDGE,"E137.MirrorCS"),sQuery(id+"F21.wireOp",EDGE,"E138.MirrorCS"),sQuery(id+"F21.wireOp",EDGE,"E139.MirrorCS"),sQuery(id+"F21.wireOp",EDGE,"E141.MirrorCS"),sQuery(id+"F21.wireOp",EDGE,"E142.MirrorCS"),sQuery(id+"F21.wireOp",EDGE,"E143.MirrorCS"),sQuery(id+"F21.wireOp",EDGE,"E144.MirrorCS"),sQuery(id+"F21.wireOp",EDGE,"E145.MirrorCS"),sQuery(id+"F21.wireOp",EDGE,"E146.MirrorCS")])]});
            booleanBodies(context, id + "F23", {"operationType" : BooleanOperationType.SUBTRACTION, "tools" : qUnion([Q0]), "targets" : qUnion([Q1, Q2]), "keepTools" : true});
        }
        {
            var Q0;
            {var subQ2=sQuery(id+"F6.wireOp",EDGE,"E52.MirrorCS");Q0=makeQuery(id+"F16.opBoolean","SPLIT",FACE,{"disambiguationData":[TD([makeQuery(id+"F12.opExtrude","CAP_FACE",FACE,{"disambiguationData":[OSD([sQuery(id+"F10.wireOp",EDGE,"E64.MirrorC"),sQuery(id+"F10.wireOp",EDGE,"E65.MirrorC")])],"isStart":true})])],"derivedFrom":makeQuery(id+"F8.boolean.opBoolean","SPLIT",FACE,{"disambiguationData":[TD([makeQuery(id+"F5.opExtrude","CAP_FACE",FACE,{"disambiguationData":[OSD([sQuery(id+"F4.wireOp",EDGE,"E28.1"),sQuery(id+"F4.wireOp",EDGE,"E30.1"),sQuery(id+"F4.wireOp",EDGE,"E30.2"),sQuery(id+"F4.wireOp",EDGE,"E30.3"),sQuery(id+"F4.wireOp",EDGE,"E30.4"),sQuery(id+"F4.wireOp",EDGE,"E30.5"),sQuery(id+"F4.wireOp",EDGE,"E30.6"),sQuery(id+"F4.wireOp",EDGE,"E30.7")])],"isStart":false})])],"derivedFrom":makeQuery(id+"F8.opExtrude","SWEPT_FACE",FACE,{"disambiguationData":[OSD([subQ2])]})})});}
            var Q1;
            {var subQ2=sQuery(id+"F6.wireOp",EDGE,"E58.MirrorCS");Q1=makeQuery(id+"F16.opBoolean","SPLIT",FACE,{"disambiguationData":[TD([makeQuery(id+"F15.opExtrude","CAP_FACE",FACE,{"disambiguationData":[OSD([sQuery(id+"F14.wireOp",EDGE,"E66.0"),sQuery(id+"F14.wireOp",EDGE,"E67.0")])],"isStart":true})])],"derivedFrom":makeQuery(id+"F8.boolean.opBoolean","SPLIT",FACE,{"disambiguationData":[TD([makeQuery(id+"F5.opExtrude","CAP_FACE",FACE,{"disambiguationData":[OSD([sQuery(id+"F4.wireOp",EDGE,"E28.1"),sQuery(id+"F4.wireOp",EDGE,"E30.1"),sQuery(id+"F4.wireOp",EDGE,"E30.2"),sQuery(id+"F4.wireOp",EDGE,"E30.3"),sQuery(id+"F4.wireOp",EDGE,"E30.4"),sQuery(id+"F4.wireOp",EDGE,"E30.5"),sQuery(id+"F4.wireOp",EDGE,"E30.6"),sQuery(id+"F4.wireOp",EDGE,"E30.7")])],"isStart":true})])],"derivedFrom":makeQuery(id+"F8.opExtrude","SWEPT_FACE",FACE,{"disambiguationData":[OSD([subQ2])]})})});}
            cPlane(context, id + "F24", {"entities" : qUnion([Q0, Q1]), "cplaneType" : CPlaneType.MID_PLANE, "offset" : 25 * mm, "width" : 150 * mm, "height" : 150 * mm});
        }
        {
            var Q0;
            Q0=qCreatedBy(id+"F24.planeOp",FACE);
            var sketch = newSketch(context, id + "F25", { "sketchPlane" : qUnion([Q0])});
            skPoint(sketch, "E147.0", {"position": v(-127.7, -41.34) * mm});
            skPoint(sketch, "E148.0", {"position": v(152.3, -41.34) * mm});
            skLineSegment(sketch, "E149", {"start": v(-140, 0) * mm, "end": v(140, 0) * mm, "construction": true});
            skLineSegment(sketch, "E150.0", {"start": v(-91, 60.5) * mm, "end": v(-91, -35.08) * mm, "construction": true});
            skPoint(sketch, "E151.orphan", {"position": v(-91, 34.92) * mm});
            skPoint(sketch, "E152.orphan", {"position": v(91, 34.92) * mm});
            skLineSegment(sketch, "E153.0", {"start": v(-65, 60.5) * mm, "end": v(-65, -55) * mm, "construction": true});
            skPoint(sketch, "E154.orphan", {"position": v(-65, 55) * mm});
            skPoint(sketch, "E155.orphan", {"position": v(65, 55) * mm});
            skLineSegment(sketch, "E156.0", {"start": v(-93, 60.5) * mm, "end": v(-93, -35.08) * mm, "construction": true});
            skLineSegment(sketch, "E157.0", {"start": v(-90, 60.5) * mm, "end": v(-90, -35.08) * mm, "construction": true});
            skLineSegment(sketch, "E158.0", {"start": v(-85, 60.5) * mm, "end": v(-85, -35.08) * mm, "construction": true});
            skLineSegment(sketch, "E159.0", {"start": v(-66, 60.5) * mm, "end": v(-66, -55) * mm, "construction": true});
            skLineSegment(sketch, "E160.0", {"start": v(-71, 60.5) * mm, "end": v(-71, -55) * mm, "construction": true});
            skLineSegment(sketch, "E161.0", {"start": v(-82.5, 60.5) * mm, "end": v(-82.5, -35.08) * mm, "construction": true});
            skLineSegment(sketch, "E162.0", {"start": v(-81.5, 60.5) * mm, "end": v(-81.5, -35.08) * mm, "construction": true});
            skLineSegment(sketch, "E163.0", {"start": v(-78.5, 60.5) * mm, "end": v(-78.5, -35.08) * mm, "construction": true});
            skLineSegment(sketch, "E164.0", {"start": v(-77.5, 60.5) * mm, "end": v(-77.5, -35.08) * mm, "construction": true});
            skLineSegment(sketch, "E165.0", {"start": v(-74.5, 60.5) * mm, "end": v(-74.5, -35.08) * mm, "construction": true});
            skLineSegment(sketch, "E166.0", {"start": v(-73.5, 60.5) * mm, "end": v(-73.5, -35.08) * mm, "construction": true});
            skLineSegment(sketch, "E167.0", {"start": v(-140, 39.5) * mm, "end": v(140, 39.5) * mm, "construction": true});
            skLineSegment(sketch, "E168", {"start": v(-90, 60.5) * mm, "end": v(-85, 60.5) * mm});
            skLineSegment(sketch, "E169", {"start": v(-85, 59.5) * mm, "end": v(-82.5, 59.5) * mm});
            skLineSegment(sketch, "E170", {"start": v(-82.5, 59.5) * mm, "end": v(-82.5, 60.5) * mm});
            skLineSegment(sketch, "E171", {"start": v(-81.5, 60.5) * mm, "end": v(-81.5, 59.5) * mm});
            skLineSegment(sketch, "E172", {"start": v(-81.5, 59.5) * mm, "end": v(-78.5, 59.5) * mm});
            skLineSegment(sketch, "E173", {"start": v(-78.5, 59.5) * mm, "end": v(-78.5, 60.5) * mm});
            skLineSegment(sketch, "E174", {"start": v(-77.5, 60.5) * mm, "end": v(-77.5, 59.5) * mm});
            skLineSegment(sketch, "E175", {"start": v(-77.5, 59.5) * mm, "end": v(-74.5, 59.5) * mm});
            skLineSegment(sketch, "E176", {"start": v(-74.5, 59.5) * mm, "end": v(-74.5, 60.5) * mm});
            skLineSegment(sketch, "E177", {"start": v(-73.5, 60.5) * mm, "end": v(-73.5, 59.5) * mm});
            skLineSegment(sketch, "E178", {"start": v(-73.5, 59.5) * mm, "end": v(-71, 59.5) * mm});
            skLineSegment(sketch, "E179", {"start": v(-71, 59.5) * mm, "end": v(-71, 60.5) * mm});
            skLineSegment(sketch, "E180", {"start": v(-66, 60.5) * mm, "end": v(-65, 59.5) * mm});
            skLineSegment(sketch, "E181", {"start": v(-65, 59.5) * mm, "end": v(-65, 0) * mm});
            skLineSegment(sketch, "E182", {"start": v(-65, 0) * mm, "end": v(-91, 0) * mm});
            skLineSegment(sketch, "E183", {"start": v(-91, 0) * mm, "end": v(-91, 34.92) * mm});
            skLineSegment(sketch, "E184", {"start": v(-85, 60.5) * mm, "end": v(-85, 59.5) * mm});
            skLineSegment(sketch, "E185", {"start": v(-82.5, 60.5) * mm, "end": v(-81.5, 60.5) * mm});
            skLineSegment(sketch, "E186", {"start": v(-78.5, 60.5) * mm, "end": v(-77.5, 60.5) * mm});
            skLineSegment(sketch, "E187", {"start": v(-74.5, 60.5) * mm, "end": v(-73.5, 60.5) * mm});
            skLineSegment(sketch, "E188", {"start": v(-71, 60.5) * mm, "end": v(-66, 60.5) * mm});
            skLineSegment(sketch, "E189", {"start": v(-95, 34.92) * mm, "end": v(-91, 34.92) * mm, "construction": true});
            skLineSegment(sketch, "E190", {"start": v(-91, 34.92) * mm, "end": v(-93, 34.92) * mm});
            skLineSegment(sketch, "E191", {"start": v(-93, 34.92) * mm, "end": v(-90, 60.5) * mm});
            skLineSegment(sketch, "E192.MirrorCS", {"start": v(74.5, 59.5) * mm, "end": v(74.5, 60.5) * mm});
            skLineSegment(sketch, "E193.MirrorCS", {"start": v(73.5, 60.5) * mm, "end": v(73.5, 59.5) * mm});
            skLineSegment(sketch, "E194.MirrorCS", {"start": v(74.5, 60.5) * mm, "end": v(73.5, 60.5) * mm});
            skLineSegment(sketch, "E195.MirrorCS", {"start": v(78.5, 59.5) * mm, "end": v(78.5, 60.5) * mm});
            skLineSegment(sketch, "E196.MirrorCS", {"start": v(81.5, 59.5) * mm, "end": v(78.5, 59.5) * mm});
            skLineSegment(sketch, "E197.MirrorCS", {"start": v(77.5, 60.5) * mm, "end": v(77.5, 59.5) * mm});
            skLineSegment(sketch, "E198.MirrorCS", {"start": v(82.5, 59.5) * mm, "end": v(82.5, 60.5) * mm});
            skLineSegment(sketch, "E199.MirrorCS", {"start": v(78.5, 60.5) * mm, "end": v(77.5, 60.5) * mm});
            skLineSegment(sketch, "E200.MirrorCS", {"start": v(81.5, 60.5) * mm, "end": v(81.5, 59.5) * mm});
            skLineSegment(sketch, "E201.MirrorCS", {"start": v(82.5, 60.5) * mm, "end": v(81.5, 60.5) * mm});
            skLineSegment(sketch, "E202.MirrorCS", {"start": v(77.5, 59.5) * mm, "end": v(74.5, 59.5) * mm});
            skLineSegment(sketch, "E203.MirrorCS", {"start": v(85, 60.5) * mm, "end": v(85, 59.5) * mm});
            skLineSegment(sketch, "E204.MirrorCS", {"start": v(71, 59.5) * mm, "end": v(71, 60.5) * mm});
            skLineSegment(sketch, "E205.MirrorCS", {"start": v(73.5, 59.5) * mm, "end": v(71, 59.5) * mm});
            skLineSegment(sketch, "E206.MirrorCS", {"start": v(85, 59.5) * mm, "end": v(82.5, 59.5) * mm});
            skLineSegment(sketch, "E207.MirrorCS", {"start": v(66, 60.5) * mm, "end": v(65, 59.5) * mm});
            skLineSegment(sketch, "E208.MirrorCS", {"start": v(91, 34.92) * mm, "end": v(93, 34.92) * mm});
            skLineSegment(sketch, "E209.MirrorCS", {"start": v(95, 34.92) * mm, "end": v(91, 34.92) * mm, "construction": true});
            skLineSegment(sketch, "E210.MirrorCS", {"start": v(91, 0) * mm, "end": v(91, 34.92) * mm});
            skLineSegment(sketch, "E211.MirrorCS", {"start": v(71, 60.5) * mm, "end": v(66, 60.5) * mm});
            skLineSegment(sketch, "E212.MirrorCS", {"start": v(90, 60.5) * mm, "end": v(85, 60.5) * mm});
            skLineSegment(sketch, "E213.MirrorCS", {"start": v(65, 0) * mm, "end": v(91, 0) * mm});
            skLineSegment(sketch, "E214.MirrorCS", {"start": v(65, 59.5) * mm, "end": v(65, 0) * mm});
            skLineSegment(sketch, "E215.MirrorCS", {"start": v(93, 34.92) * mm, "end": v(90, 60.5) * mm});
            skLineSegment(sketch, "E216.0", {"start": v(-95, 34.92) * mm, "end": v(-95, -35.08) * mm, "construction": true});
            skSolve(sketch);
        }
        {
            var Q0;
            Q0=qSketchRegion(id+"F25",true);
            var Q1;
            Q1=sQuery(id+"F25.wireOp",EDGE,"E149");
            revolve(context, id + "F26", {"entities" : qUnion([Q0]), "axis" : qUnion([Q1]), "revolveType" : RevolveType.FULL});
        }
        {
            var Q0;
            Q0=makeQuery(id+"F5.opExtrude","SWEPT_BODY",BODY,{"disambiguationData":[OSD([sQuery(id+"F4.wireOp",EDGE,"E28.1"),sQuery(id+"F4.wireOp",EDGE,"E30.1"),sQuery(id+"F4.wireOp",EDGE,"E30.2"),sQuery(id+"F4.wireOp",EDGE,"E30.3"),sQuery(id+"F4.wireOp",EDGE,"E30.4"),sQuery(id+"F4.wireOp",EDGE,"E30.5"),sQuery(id+"F4.wireOp",EDGE,"E30.6"),sQuery(id+"F4.wireOp",EDGE,"E30.7")])]});
            var Q1;
            Q1=makeQuery(id+"F26.opRevolve","SWEPT_BODY",BODY,{"disambiguationData":[OSD([sQuery(id+"F25.wireOp",EDGE,"E168"),sQuery(id+"F25.wireOp",EDGE,"E169"),sQuery(id+"F25.wireOp",EDGE,"E170"),sQuery(id+"F25.wireOp",EDGE,"E171"),sQuery(id+"F25.wireOp",EDGE,"E172"),sQuery(id+"F25.wireOp",EDGE,"E173"),sQuery(id+"F25.wireOp",EDGE,"E174"),sQuery(id+"F25.wireOp",EDGE,"E175"),sQuery(id+"F25.wireOp",EDGE,"E176"),sQuery(id+"F25.wireOp",EDGE,"E177"),sQuery(id+"F25.wireOp",EDGE,"E178"),sQuery(id+"F25.wireOp",EDGE,"E179"),sQuery(id+"F25.wireOp",EDGE,"E180"),sQuery(id+"F25.wireOp",EDGE,"E181"),sQuery(id+"F25.wireOp",EDGE,"E182"),sQuery(id+"F25.wireOp",EDGE,"E183"),sQuery(id+"F25.wireOp",EDGE,"E184"),sQuery(id+"F25.wireOp",EDGE,"E185"),sQuery(id+"F25.wireOp",EDGE,"E186"),sQuery(id+"F25.wireOp",EDGE,"E187"),sQuery(id+"F25.wireOp",EDGE,"E188"),sQuery(id+"F25.wireOp",EDGE,"E190"),sQuery(id+"F25.wireOp",EDGE,"E191")])]});
            var Q2;
            Q2=makeQuery(id+"F26.opRevolve","SWEPT_BODY",BODY,{"disambiguationData":[OSD([sQuery(id+"F25.wireOp",EDGE,"E192.MirrorCS"),sQuery(id+"F25.wireOp",EDGE,"E193.MirrorCS"),sQuery(id+"F25.wireOp",EDGE,"E194.MirrorCS"),sQuery(id+"F25.wireOp",EDGE,"E195.MirrorCS"),sQuery(id+"F25.wireOp",EDGE,"E196.MirrorCS"),sQuery(id+"F25.wireOp",EDGE,"E197.MirrorCS"),sQuery(id+"F25.wireOp",EDGE,"E198.MirrorCS"),sQuery(id+"F25.wireOp",EDGE,"E199.MirrorCS"),sQuery(id+"F25.wireOp",EDGE,"E200.MirrorCS"),sQuery(id+"F25.wireOp",EDGE,"E201.MirrorCS"),sQuery(id+"F25.wireOp",EDGE,"E202.MirrorCS"),sQuery(id+"F25.wireOp",EDGE,"E203.MirrorCS"),sQuery(id+"F25.wireOp",EDGE,"E204.MirrorCS"),sQuery(id+"F25.wireOp",EDGE,"E205.MirrorCS"),sQuery(id+"F25.wireOp",EDGE,"E206.MirrorCS"),sQuery(id+"F25.wireOp",EDGE,"E207.MirrorCS"),sQuery(id+"F25.wireOp",EDGE,"E208.MirrorCS"),sQuery(id+"F25.wireOp",EDGE,"E210.MirrorCS"),sQuery(id+"F25.wireOp",EDGE,"E211.MirrorCS"),sQuery(id+"F25.wireOp",EDGE,"E212.MirrorCS"),sQuery(id+"F25.wireOp",EDGE,"E213.MirrorCS"),sQuery(id+"F25.wireOp",EDGE,"E214.MirrorCS"),sQuery(id+"F25.wireOp",EDGE,"E215.MirrorCS")])]});
            booleanBodies(context, id + "F27", {"operationType" : BooleanOperationType.SUBTRACTION, "tools" : qUnion([Q0]), "targets" : qUnion([Q1, Q2]), "keepTools" : true});
        }
        {
            var Q0;
            Q0=makeQuery(id+"F5.opExtrude","SWEPT_BODY",BODY,{"disambiguationData":[OSD([sQuery(id+"F4.wireOp",EDGE,"E28.1"),sQuery(id+"F4.wireOp",EDGE,"E30.1"),sQuery(id+"F4.wireOp",EDGE,"E30.2"),sQuery(id+"F4.wireOp",EDGE,"E30.3"),sQuery(id+"F4.wireOp",EDGE,"E30.4"),sQuery(id+"F4.wireOp",EDGE,"E30.5"),sQuery(id+"F4.wireOp",EDGE,"E30.6"),sQuery(id+"F4.wireOp",EDGE,"E30.7")])]});
            deleteBodies(context, id + "F28", {"entities" : qUnion([Q0])});
        }
        {
            var Q0;
            Q0=makeQuery(id+"F12.opExtrude","SWEPT_BODY",BODY,{"disambiguationData":[OSD([sQuery(id+"F10.wireOp",EDGE,"E64.MirrorC"),sQuery(id+"F10.wireOp",EDGE,"E65.MirrorC")])]});
            deleteBodies(context, id + "F29", {"entities" : qUnion([Q0])});
        }
        {
            var Q0;
            Q0=makeQuery(id+"F15.opExtrude","SWEPT_BODY",BODY,{"disambiguationData":[OSD([sQuery(id+"F14.wireOp",EDGE,"E66.0"),sQuery(id+"F14.wireOp",EDGE,"E67.0")])]});
            deleteBodies(context, id + "F30", {"entities" : qUnion([Q0])});
        }
        {
            var Q0;
            Q0=makeQuery(id+"F15.opExtrude","SWEPT_BODY",BODY,{"disambiguationData":[OSD([sQuery(id+"F14.wireOp",EDGE,"E68.0"),sQuery(id+"F14.wireOp",EDGE,"E69.0")])]});
            deleteBodies(context, id + "F31", {"entities" : qUnion([Q0])});
        }
        {
            var Q0;
            Q0=makeQuery(id+"F22.opRevolve","SWEPT_BODY",BODY,{"disambiguationData":[OSD([sQuery(id+"F21.wireOp",EDGE,"E123.MirrorCS"),sQuery(id+"F21.wireOp",EDGE,"E124.MirrorCS"),sQuery(id+"F21.wireOp",EDGE,"E125.MirrorCS"),sQuery(id+"F21.wireOp",EDGE,"E126.MirrorCS"),sQuery(id+"F21.wireOp",EDGE,"E127.MirrorCS"),sQuery(id+"F21.wireOp",EDGE,"E128.MirrorCS"),sQuery(id+"F21.wireOp",EDGE,"E129.MirrorCS"),sQuery(id+"F21.wireOp",EDGE,"E130.MirrorCS"),sQuery(id+"F21.wireOp",EDGE,"E131.MirrorCS"),sQuery(id+"F21.wireOp",EDGE,"E132.MirrorCS"),sQuery(id+"F21.wireOp",EDGE,"E133.MirrorCS"),sQuery(id+"F21.wireOp",EDGE,"E134.MirrorCS"),sQuery(id+"F21.wireOp",EDGE,"E135.MirrorCS"),sQuery(id+"F21.wireOp",EDGE,"E136.MirrorCS"),sQuery(id+"F21.wireOp",EDGE,"E137.MirrorCS"),sQuery(id+"F21.wireOp",EDGE,"E138.MirrorCS"),sQuery(id+"F21.wireOp",EDGE,"E139.MirrorCS"),sQuery(id+"F21.wireOp",EDGE,"E141.MirrorCS"),sQuery(id+"F21.wireOp",EDGE,"E142.MirrorCS"),sQuery(id+"F21.wireOp",EDGE,"E143.MirrorCS"),sQuery(id+"F21.wireOp",EDGE,"E144.MirrorCS"),sQuery(id+"F21.wireOp",EDGE,"E145.MirrorCS"),sQuery(id+"F21.wireOp",EDGE,"E146.MirrorCS")])]});
            var Q1;
            Q1=makeQuery(id+"F26.opRevolve","SWEPT_BODY",BODY,{"disambiguationData":[OSD([sQuery(id+"F25.wireOp",EDGE,"E168"),sQuery(id+"F25.wireOp",EDGE,"E169"),sQuery(id+"F25.wireOp",EDGE,"E170"),sQuery(id+"F25.wireOp",EDGE,"E171"),sQuery(id+"F25.wireOp",EDGE,"E172"),sQuery(id+"F25.wireOp",EDGE,"E173"),sQuery(id+"F25.wireOp",EDGE,"E174"),sQuery(id+"F25.wireOp",EDGE,"E175"),sQuery(id+"F25.wireOp",EDGE,"E176"),sQuery(id+"F25.wireOp",EDGE,"E177"),sQuery(id+"F25.wireOp",EDGE,"E178"),sQuery(id+"F25.wireOp",EDGE,"E179"),sQuery(id+"F25.wireOp",EDGE,"E180"),sQuery(id+"F25.wireOp",EDGE,"E181"),sQuery(id+"F25.wireOp",EDGE,"E182"),sQuery(id+"F25.wireOp",EDGE,"E183"),sQuery(id+"F25.wireOp",EDGE,"E184"),sQuery(id+"F25.wireOp",EDGE,"E185"),sQuery(id+"F25.wireOp",EDGE,"E186"),sQuery(id+"F25.wireOp",EDGE,"E187"),sQuery(id+"F25.wireOp",EDGE,"E188"),sQuery(id+"F25.wireOp",EDGE,"E190"),sQuery(id+"F25.wireOp",EDGE,"E191")])]});
            var Q2;
            Q2=makeQuery(id+"F26.opRevolve","SWEPT_BODY",BODY,{"disambiguationData":[OSD([sQuery(id+"F25.wireOp",EDGE,"E192.MirrorCS"),sQuery(id+"F25.wireOp",EDGE,"E193.MirrorCS"),sQuery(id+"F25.wireOp",EDGE,"E194.MirrorCS"),sQuery(id+"F25.wireOp",EDGE,"E195.MirrorCS"),sQuery(id+"F25.wireOp",EDGE,"E196.MirrorCS"),sQuery(id+"F25.wireOp",EDGE,"E197.MirrorCS"),sQuery(id+"F25.wireOp",EDGE,"E198.MirrorCS"),sQuery(id+"F25.wireOp",EDGE,"E199.MirrorCS"),sQuery(id+"F25.wireOp",EDGE,"E200.MirrorCS"),sQuery(id+"F25.wireOp",EDGE,"E201.MirrorCS"),sQuery(id+"F25.wireOp",EDGE,"E202.MirrorCS"),sQuery(id+"F25.wireOp",EDGE,"E203.MirrorCS"),sQuery(id+"F25.wireOp",EDGE,"E204.MirrorCS"),sQuery(id+"F25.wireOp",EDGE,"E205.MirrorCS"),sQuery(id+"F25.wireOp",EDGE,"E206.MirrorCS"),sQuery(id+"F25.wireOp",EDGE,"E207.MirrorCS"),sQuery(id+"F25.wireOp",EDGE,"E208.MirrorCS"),sQuery(id+"F25.wireOp",EDGE,"E210.MirrorCS"),sQuery(id+"F25.wireOp",EDGE,"E211.MirrorCS"),sQuery(id+"F25.wireOp",EDGE,"E212.MirrorCS"),sQuery(id+"F25.wireOp",EDGE,"E213.MirrorCS"),sQuery(id+"F25.wireOp",EDGE,"E214.MirrorCS"),sQuery(id+"F25.wireOp",EDGE,"E215.MirrorCS")])]});
            deleteBodies(context, id + "F32", {"entities" : qUnion([Q0, Q1, Q2])});
        }
    });
